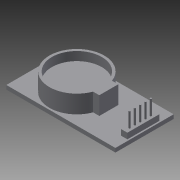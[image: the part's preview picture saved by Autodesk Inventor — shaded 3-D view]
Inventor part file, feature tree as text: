
AUTODESK INVENTOR PART (.ipt)
format: ipt  version: 2016 (Build 200138000, 138)  size: 190,464 bytes
history: native  units: in
note: dims shown in document units (in); Inventor stores cm internally (conversion verified against a paired STEP export)
features: sketch x10, extrude x9, fillet x1
ambient origin geometry x8: Origin, YZ Plane, XZ Plane, XY Plane, X Axis, Y Axis, Z Axis, Center Point
bodies: Solid1 (feature_tree)
feature tree (20):
  extrude  "Extrusion1"  Depth=0.9213in
  extrude  "Extrusion2"  Depth=0.5039in
  extrude  "Extrusion3"  Depth=0.0984in
  extrude  "Extrusion4"  Depth=0.0906in TaperAngle=0.0deg
  extrude  "Extrusion5"  Depth=0.0276in
  extrude  "Extrusion6"  Depth=0.0276in
  sketch  "Sketch7"  dims[d16=0.0276in d17=0.0276in]
  extrude  "Extrusion7"  Depth=0.0276in
  extrude  "Extrusion8"  Depth=0.0839in
  fillet  "Fillet1"  Radius=0.0839in
  extrude  "Extrusion9"  Depth=0.2362in TaperAngle=0.0deg
  sketch  "Sketch1"  dims[d0=1.7244in d1=0.9213in]
  sketch  "Sketch2"  dims[d2=0.063in d3=0.0in d6=0.5039in]
  sketch  "Sketch3"  dims[d7=0.0236in d8=0.0984in]
  sketch  "Sketch4"  dims[d9=0.2126in d10=0.0906in d11=0.0in]
  sketch  "Sketch5"  dims[d12=0.0839in d13=0.0276in]
  sketch  "Sketch6"  dims[d14=0.0276in d15=0.0276in]
  sketch  "Sketch8"  dims[d19=0.0839in d20=0.0839in d21=0.0839in]
  sketch  "Sketch10"  dims[d22=0.0839in d23=0.2362in d24=0.0in]
  sketch  "Sketch11"  dims[d25=0.8661in d28=0.2835in d29=0.0in d30=0.2992in d31=0.0984in d32=0.0984in d33=0.2835in d34=0.0in d35=0.7874in d36=0.1378in d37=0.0in d38=0.0827in d39=0.3937in d40=0.3937in d41=0.2953in d42=0.3465in d43=0.0in d44=0.5512in d45=0.4606in d46=0.1181in d47=0.3543in d48=0.1181in d49=0.315in d50=0.0in d51=0.0787in d52=0.1181in d53=0.1181in d54=0.8425in d55=0.1181in d56=1.4252in d57=0.1181in d58=0.1181in d59=0.1181in d60=0.7244in d61=0.0984in d62=0.0984in d64=1.4252in d65=0.315in d66=0.0in]
